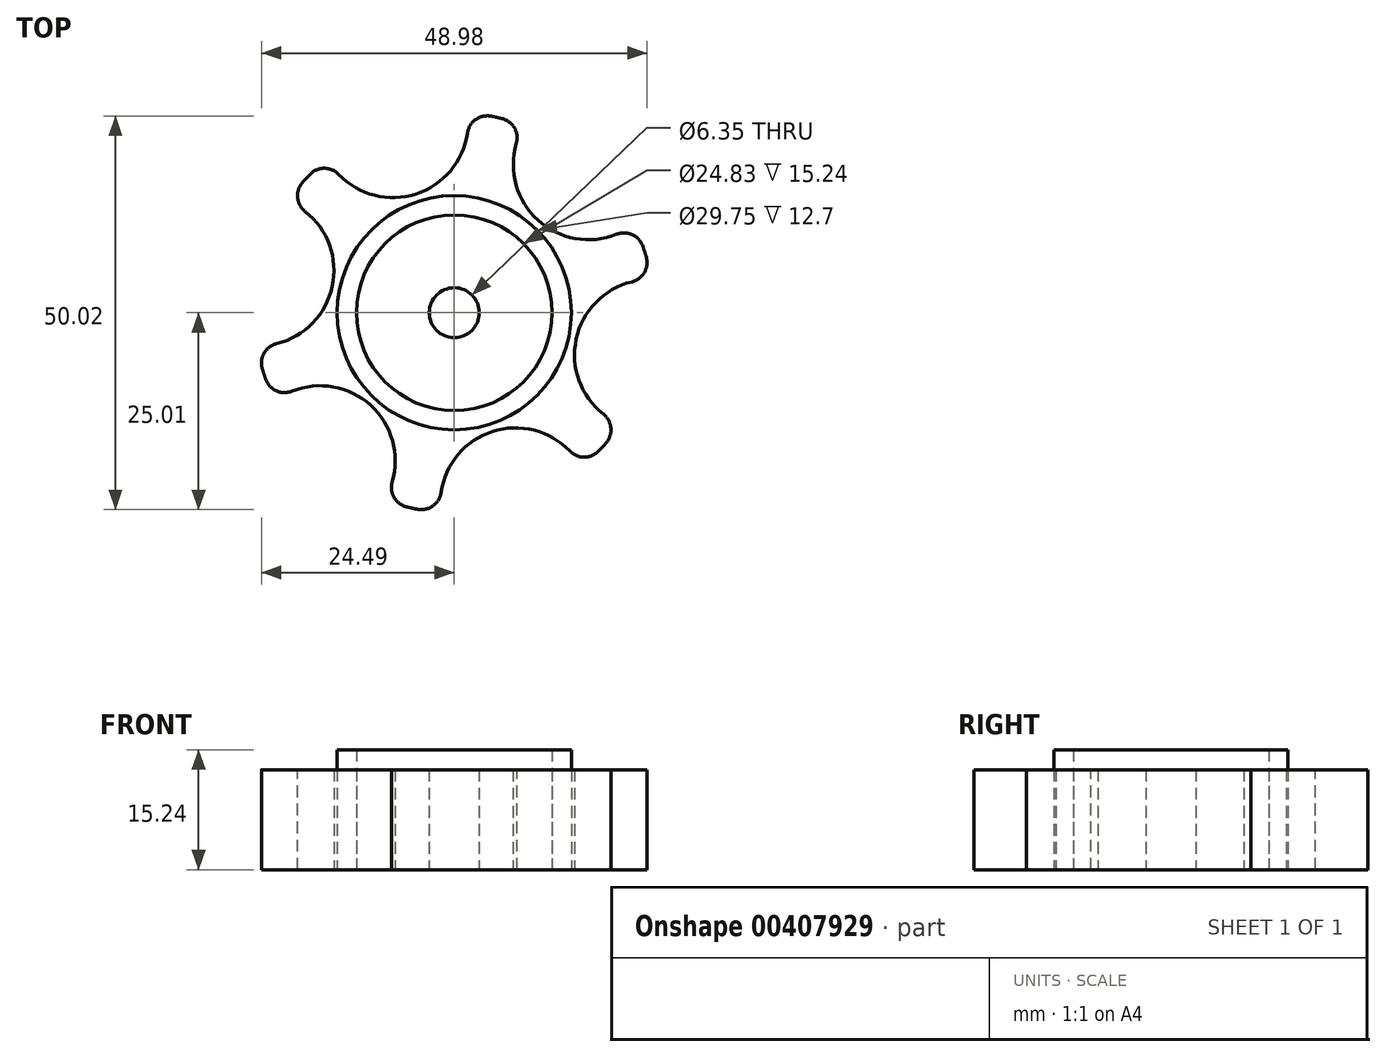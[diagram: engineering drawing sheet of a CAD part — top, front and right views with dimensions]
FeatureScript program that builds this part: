
annotation { "Feature Type Name" : "Feature", "Feature Type Description" : "" }
export const myFeature = defineFeature(function(context is Context, id is Id, definition is map)
    precondition{}
    {
        {
            var Q0;
            Q0=qCreatedBy(makeId("Top.planeOp"),FACE);
            var sketch = newSketch(context, id + "F0", { "sketchPlane" : qUnion([Q0])});
            skCircle(sketch, "E0", {"center": v(0, 0) * mm, "radius": 25.4 * mm});
            skCircle(sketch, "E1", {"center": v(17.05, 18.83) * mm, "radius": 9.55 * mm});
            skCircle(sketch, "E2.1.0", {"center": v(-7.78, 24.18) * mm, "radius": 9.55 * mm});
            skCircle(sketch, "E2.2.0", {"center": v(-24.83, 5.35) * mm, "radius": 9.55 * mm});
            skCircle(sketch, "E2.3.0", {"center": v(-17.05, -18.83) * mm, "radius": 9.55 * mm});
            skCircle(sketch, "E2.4.0", {"center": v(7.78, -24.18) * mm, "radius": 9.55 * mm});
            skCircle(sketch, "E2.5.0", {"center": v(24.83, -5.35) * mm, "radius": 9.55 * mm});
            skCircle(sketch, "E3", {"center": v(0, 0) * mm, "radius": 3.18 * mm});
            skCircle(sketch, "E4", {"center": v(0, 0) * mm, "radius": 12.42 * mm});
            skCircle(sketch, "E5", {"center": v(0, 0) * mm, "radius": 14.87 * mm});
            skSolve(sketch);
        }
        {
            var Q0;
            {var subQ1=sQuery(id+"F0.wireOp",EDGE,"E0");var subQ10=sQuery(id+"F0.wireOp",EDGE,"E1");var subQ11=makeQuery(id+"F0.imprint","INTERSECT",VERTEX,{"disambiguationData":[OD(0.0)],"derivedFrom":[subQ1,subQ10]});Q0=makeQuery(id+"F0.imprint","IMPRINT",FACE,{"disambiguationData":[TD([[makeQuery(id+"F0.imprint","IMPRINT",EDGE,{"disambiguationData":[TD([[subQ11,1.0]])],"derivedFrom":subQ1}),1.0]])]});}
            extrude(context, id + "F1", {"entities" : qUnion([Q0]), "depth" : 12.7 * mm});
        }
        {
            var Q0;
            {var subQ0=sQuery(id+"F0.wireOp",EDGE,"E2.1.0");var subQ1=sQuery(id+"F0.wireOp",EDGE,"E0");Q0=makeQuery(id+"F1.opExtrude","SWEPT_EDGE",EDGE,{"disambiguationData":[OSD([subQ1,subQ0]),TDD([makeQuery(id+"F0.imprint","INTERSECT",VERTEX,{"disambiguationData":[OD(0.0)],"derivedFrom":[subQ1,subQ0]})])]});}
            var Q1;
            {var subQ0=sQuery(id+"F0.wireOp",EDGE,"E1");var subQ1=sQuery(id+"F0.wireOp",EDGE,"E0");Q1=makeQuery(id+"F1.opExtrude","SWEPT_EDGE",EDGE,{"disambiguationData":[OSD([subQ1,subQ0]),TDD([makeQuery(id+"F0.imprint","INTERSECT",VERTEX,{"disambiguationData":[OD(1.0)],"derivedFrom":[subQ1,subQ0]})])]});}
            var Q2;
            {var subQ0=sQuery(id+"F0.wireOp",EDGE,"E2.1.0");var subQ1=sQuery(id+"F0.wireOp",EDGE,"E0");Q2=makeQuery(id+"F1.opExtrude","SWEPT_EDGE",EDGE,{"disambiguationData":[OSD([subQ1,subQ0]),TDD([makeQuery(id+"F0.imprint","INTERSECT",VERTEX,{"disambiguationData":[OD(1.0)],"derivedFrom":[subQ1,subQ0]})])]});}
            var Q3;
            {var subQ0=sQuery(id+"F0.wireOp",EDGE,"E2.2.0");var subQ1=sQuery(id+"F0.wireOp",EDGE,"E0");Q3=makeQuery(id+"F1.opExtrude","SWEPT_EDGE",EDGE,{"disambiguationData":[OSD([subQ1,subQ0]),TDD([makeQuery(id+"F0.imprint","INTERSECT",VERTEX,{"disambiguationData":[OD(0.0)],"derivedFrom":[subQ1,subQ0]})])]});}
            var Q4;
            {var subQ0=sQuery(id+"F0.wireOp",EDGE,"E2.2.0");var subQ1=sQuery(id+"F0.wireOp",EDGE,"E0");Q4=makeQuery(id+"F1.opExtrude","SWEPT_EDGE",EDGE,{"disambiguationData":[OSD([subQ1,subQ0]),TDD([makeQuery(id+"F0.imprint","INTERSECT",VERTEX,{"disambiguationData":[OD(1.0)],"derivedFrom":[subQ1,subQ0]})])]});}
            var Q5;
            {var subQ0=sQuery(id+"F0.wireOp",EDGE,"E2.5.0");var subQ1=sQuery(id+"F0.wireOp",EDGE,"E0");Q5=makeQuery(id+"F1.opExtrude","SWEPT_EDGE",EDGE,{"disambiguationData":[OSD([subQ1,subQ0]),TDD([makeQuery(id+"F0.imprint","INTERSECT",VERTEX,{"disambiguationData":[OD(0.0)],"derivedFrom":[subQ1,subQ0]})])]});}
            var Q6;
            {var subQ0=sQuery(id+"F0.wireOp",EDGE,"E1");var subQ1=sQuery(id+"F0.wireOp",EDGE,"E0");Q6=makeQuery(id+"F1.opExtrude","SWEPT_EDGE",EDGE,{"disambiguationData":[OSD([subQ1,subQ0]),TDD([makeQuery(id+"F0.imprint","INTERSECT",VERTEX,{"disambiguationData":[OD(0.0)],"derivedFrom":[subQ1,subQ0]})])]});}
            var Q7;
            {var subQ0=sQuery(id+"F0.wireOp",EDGE,"E2.5.0");var subQ1=sQuery(id+"F0.wireOp",EDGE,"E0");Q7=makeQuery(id+"F1.opExtrude","SWEPT_EDGE",EDGE,{"disambiguationData":[OSD([subQ1,subQ0]),TDD([makeQuery(id+"F0.imprint","INTERSECT",VERTEX,{"disambiguationData":[OD(1.0)],"derivedFrom":[subQ1,subQ0]})])]});}
            var Q8;
            {var subQ0=sQuery(id+"F0.wireOp",EDGE,"E2.4.0");var subQ1=sQuery(id+"F0.wireOp",EDGE,"E0");Q8=makeQuery(id+"F1.opExtrude","SWEPT_EDGE",EDGE,{"disambiguationData":[OSD([subQ1,subQ0]),TDD([makeQuery(id+"F0.imprint","INTERSECT",VERTEX,{"disambiguationData":[OD(1.0)],"derivedFrom":[subQ1,subQ0]})])]});}
            var Q9;
            {var subQ0=sQuery(id+"F0.wireOp",EDGE,"E2.4.0");var subQ1=sQuery(id+"F0.wireOp",EDGE,"E0");Q9=makeQuery(id+"F1.opExtrude","SWEPT_EDGE",EDGE,{"disambiguationData":[OSD([subQ1,subQ0]),TDD([makeQuery(id+"F0.imprint","INTERSECT",VERTEX,{"disambiguationData":[OD(0.0)],"derivedFrom":[subQ1,subQ0]})])]});}
            var Q10;
            {var subQ0=sQuery(id+"F0.wireOp",EDGE,"E2.3.0");var subQ1=sQuery(id+"F0.wireOp",EDGE,"E0");Q10=makeQuery(id+"F1.opExtrude","SWEPT_EDGE",EDGE,{"disambiguationData":[OSD([subQ1,subQ0]),TDD([makeQuery(id+"F0.imprint","INTERSECT",VERTEX,{"disambiguationData":[OD(1.0)],"derivedFrom":[subQ1,subQ0]})])]});}
            var Q11;
            {var subQ0=sQuery(id+"F0.wireOp",EDGE,"E2.3.0");var subQ1=sQuery(id+"F0.wireOp",EDGE,"E0");Q11=makeQuery(id+"F1.opExtrude","SWEPT_EDGE",EDGE,{"disambiguationData":[OSD([subQ1,subQ0]),TDD([makeQuery(id+"F0.imprint","INTERSECT",VERTEX,{"disambiguationData":[OD(0.0)],"derivedFrom":[subQ1,subQ0]})])]});}
            fillet(context, id + "F2", {"entities" : qUnion([Q0, Q1, Q2, Q3, Q4, Q5, Q6, Q7, Q8, Q9, Q10, Q11]), "radius" : 2.54 * mm, "tangentPropagation" : true, "allowEdgeOverflow" : false});
        }
        {
            var Q0;
            Q0=makeQuery(id+"F0.imprint","IMPRINT",FACE,{"disambiguationData":[TD([[makeQuery(id+"F0.imprint","IMPRINT",EDGE,{"derivedFrom":sQuery(id+"F0.wireOp",EDGE,"E3")}),-1.0]])]});
            extrude(context, id + "F3", {"entities" : qUnion([Q0]), "depth" : 12.7 * mm});
        }
        {
            var Q0;
            Q0=makeQuery(id+"F0.imprint","IMPRINT",FACE,{"disambiguationData":[TD([[makeQuery(id+"F0.imprint","IMPRINT",EDGE,{"derivedFrom":sQuery(id+"F0.wireOp",EDGE,"E4")}),-1.0]])]});
            extrude(context, id + "F4", {"entities" : qUnion([Q0]), "depth" : 15.24 * mm});
        }
    });
